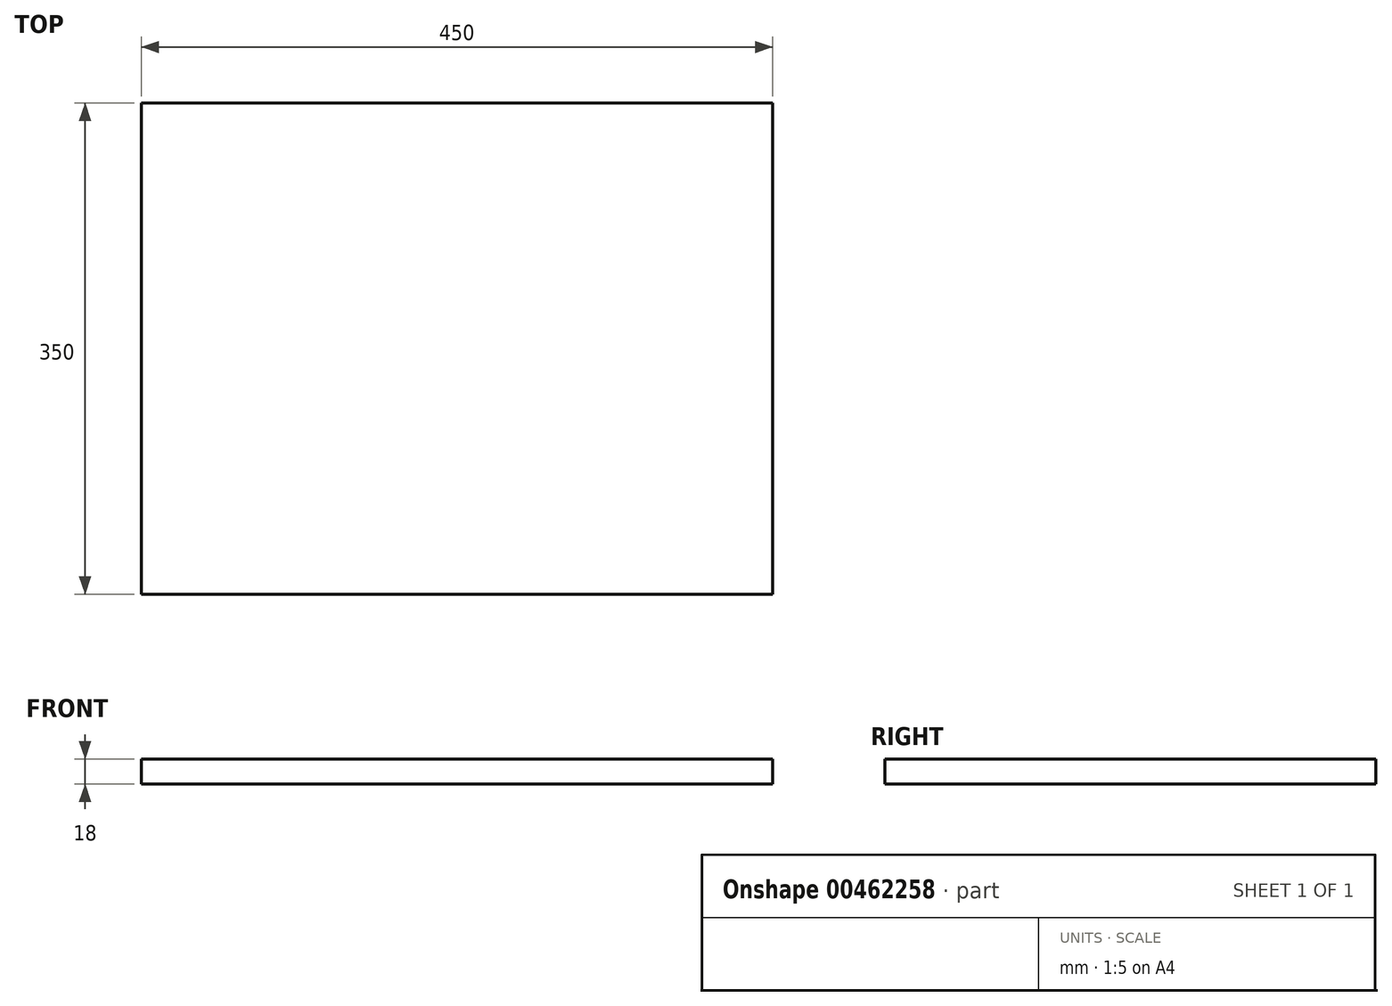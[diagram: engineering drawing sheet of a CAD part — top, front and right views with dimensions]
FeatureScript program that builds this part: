
annotation { "Feature Type Name" : "Feature", "Feature Type Description" : "" }
export const myFeature = defineFeature(function(context is Context, id is Id, definition is map)
    precondition{}
    {
        {
            var Q0;
            Q0=qCreatedBy(makeId("Top.planeOp"),FACE);
            var sketch = newSketch(context, id + "F0", { "sketchPlane" : qUnion([Q0])});
            skLineSegment(sketch, "E0.bottom", {"start": v(240, -175) * mm, "end": v(-210, -175) * mm});
            skLineSegment(sketch, "E0.top", {"start": v(240, 175) * mm, "end": v(-210, 175) * mm});
            skLineSegment(sketch, "E0.left", {"start": v(240, -175) * mm, "end": v(240, 175) * mm});
            skLineSegment(sketch, "E0.right", {"start": v(-210, -175) * mm, "end": v(-210, 175) * mm});
            skPoint(sketch, "E0.middle", {"position": v(15, 0) * mm});
            skSolve(sketch);
        }
        {
            var Q0;
            Q0=makeQuery(id+"F0.imprint","IMPRINT",FACE,{"disambiguationData":[TD([[makeQuery(id+"F0.imprint","IMPRINT",EDGE,{"derivedFrom":sQuery(id+"F0.wireOp",EDGE,"E0.bottom")}),-1.0]])]});
            extrude(context, id + "F1", {"entities" : qUnion([Q0]), "depth" : 18 * mm});
        }
    });
